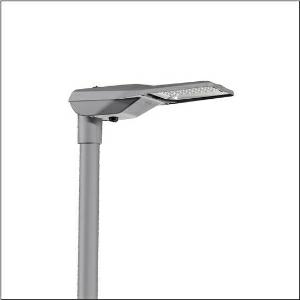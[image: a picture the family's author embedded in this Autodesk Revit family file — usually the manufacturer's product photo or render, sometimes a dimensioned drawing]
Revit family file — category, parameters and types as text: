
# Revit family: streetlight_sl_21_mini___p0_8a_5xe2u33t08hb_848e
name_source: partatom
category: Lighting Fixtures
units: mm (PartAtom-declared; Revit-internal decimal feet)

## family parameters
Cut with Voids When Loaded = No
Host = Face
Light Source = No
Part Type = Normal
Room Calculation Point = No
Round Connector Dimension = Use Diameter
Shared = No

## types (1)
- --- (1 x LED, 9120 lm, 66 W, 3000K)
    Apparent Load = 66 VA
    CIE Flux Codes = 33 69 96 100 100
    Color Rendering = 70
    Color Temperature = 3000K
    Default Elevation = 1800 mm
    Description = Streetlight SL 21 mini, mast luminaire, primary light control with lens, of PMMA, primary optical cover: cover, of toughened safety glass, transparent, light distribution: P0.8a, light emission: direct distribution, primary light characteristic: asymmetric, installation type: post-top, side-entry, LED, High Power LED, rated luminous flux: 9.120lm, luminous efficacy: 138lm/W, light colour: 730, colour temperature: 3000K, control gear: D4i, control: pre-setting: logarithmic dimming characteristic, flexible luminous flux parameterisation, time-dependent luminous flux control, constant luminous flux control, overheat protection, mains connection: 220..240V, AC, 50/60Hz, start of lifetime: 66W, end of service life: 69W, reduction: 30W, luminaire housing, of diecast aluminium, powder-coated, SITECO metallic grey (DB 702S), corrosivity category C5 high according to DIN EN ISO 12944, multi-level sealing system, sealing non-destructively replaceable, inclination adjustable: 0°, 5°, 10°, 15°, please order mast flange separately, length: 628mm, width: 235mm, height: 110mm, mast flange for spigot size: 42mm (side-entry): 5XC10008XM4, 60/48mm (side-entry/post-top): 5XC10108XM2, 76/60mm (side-entry/post-top): 5XC10108XM1, mounting height: 4..8m, Smart Interface below and above, protection rating (complete): IP66, insulation class (complete): insulation class II (safety insulation), certification: CE, ENEC, ENEC+, VDE, impact resistance: IK10, permissible operating ambient temperature for outdoor applications: -40..+50°C, standard-compliant lighting for roads and squares, packaging unit: 1 piece

Light Distribution: P0.8a
    Height = 110 mm
    Lamp = 1 x LED
    Lamp Light Flux = 9120 lm
    Lamp Power = 66 W
    Lamp count = 1
    Length = 625 mm
    Luminous efficacy = 138 lm/W
    Manufacturer = Siteco
    ModVariant = No
    Model = 5XE2U33T08HB
    Number of Poles = 1
    OnlyDefault = Yes
    Power Factor = 1
    Product Name = Streetlight SL 21 mini | P0.8a
    Product group = mast luminaire | pylon top
    ProductGroupID = 6100
    Protection Class = Protection class II
    Protection Degree = IP 66
    RLX_Detail_Level = 1
    RLX_Emergency_Light_Flux = 0 lm
    RLX_Emergency_Type = 0
    RLX_Emergency_Type_DB = No
    RlxData = <blob elided: 92033 chars, md5=7d1e53be>
    Socket = socket
    Standby Power = 0 W
    System Light Flux = 9120 lm
    System Power = 66 W
    Type Comments = factory setting: luminous flux: 100 % | dim-lin: 254 | 670 mA
    Type Image = l_1003514.jpg
    URL = http://relux.com
    VarID = @adj_080219
    Voltage = 0 V
    Weight = 0.00 kg
    Width = 234 mm

## geometry (parser evidence)
native form markers: Blend x4, Sweep x10
no freeform markers — native parametric forms only
